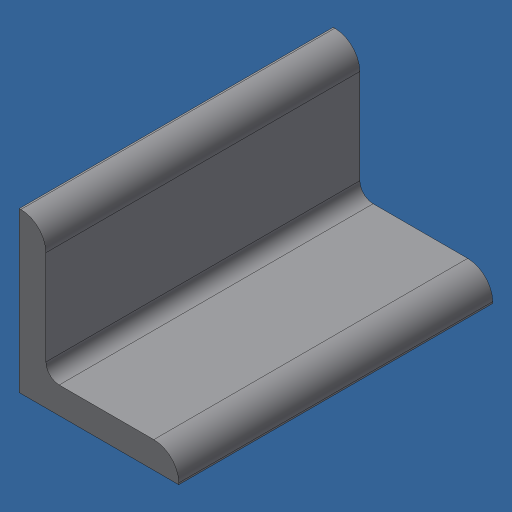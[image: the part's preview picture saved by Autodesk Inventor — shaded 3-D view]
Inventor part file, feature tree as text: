
AUTODESK INVENTOR PART (.ipt)
format: ipt  version: 2024.3 (Build 283343000, 343)  size: 139,264 bytes
history: native  units: mm (DEFAULTED — no unit token found)
features: other x1, extrude x1
ambient origin geometry x8: Origin, YZ Plane, XZ Plane, XY Plane, X Axis, Y Axis, Z Axis, Center Point
bodies: Body1 (feature_tree)
feature tree (2):
  other  "Finish - None"
  extrude  "6" X 6" X 1""  Depth=25.4mm
